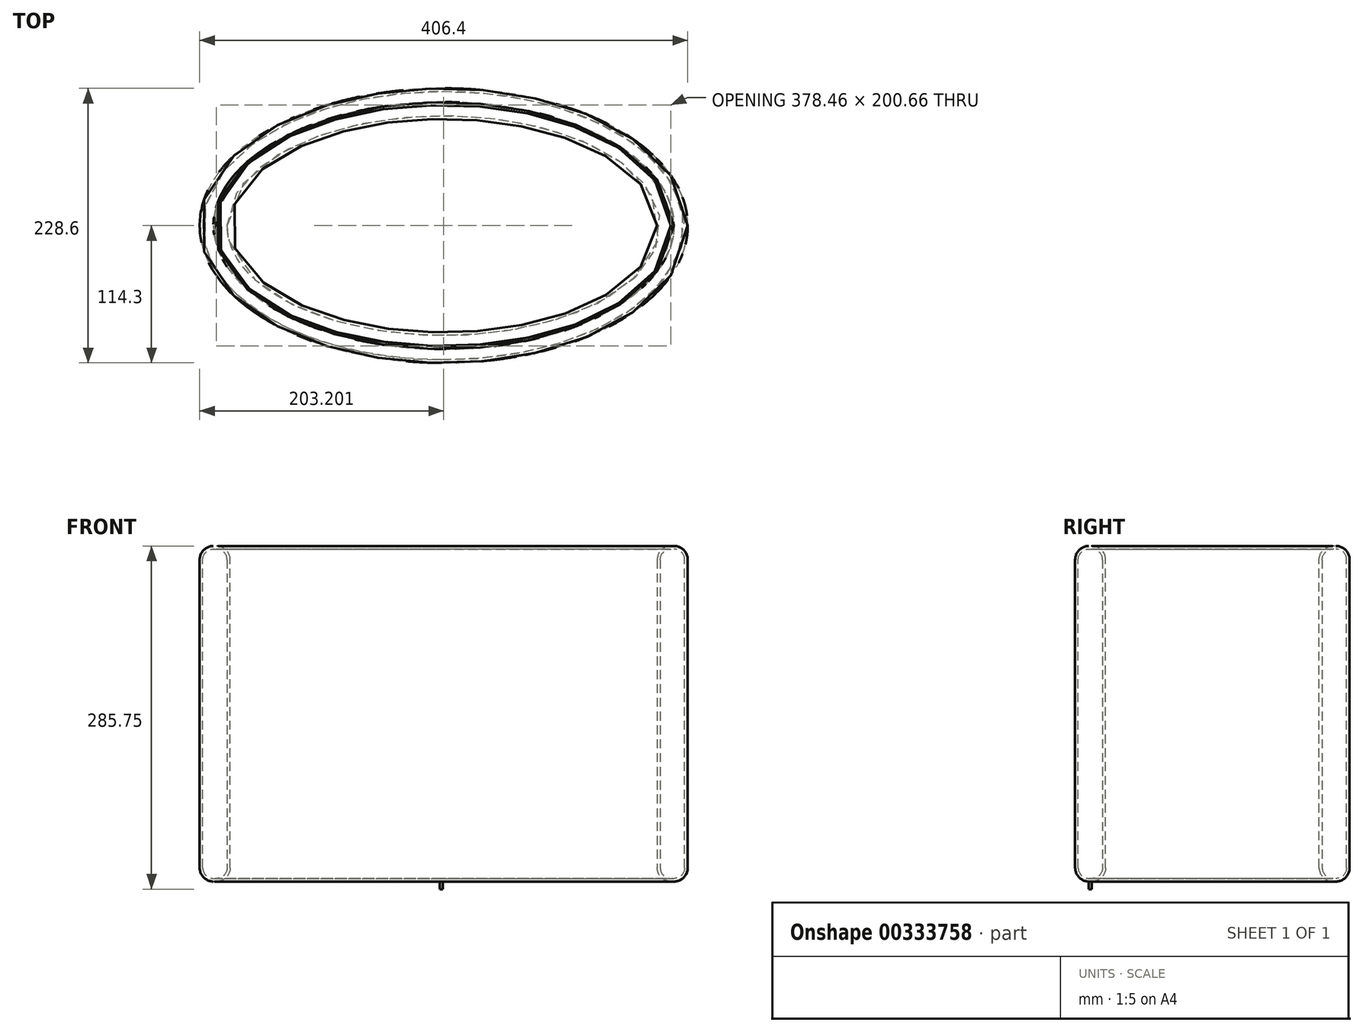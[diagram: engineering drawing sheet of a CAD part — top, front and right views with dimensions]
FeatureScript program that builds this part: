
annotation { "Feature Type Name" : "Feature", "Feature Type Description" : "" }
export const myFeature = defineFeature(function(context is Context, id is Id, definition is map)
    precondition{}
    {
        {
            var Q0;
            Q0=qCreatedBy(makeId("Top.planeOp"),FACE);
            var sketch = newSketch(context, id + "F0", { "sketchPlane" : qUnion([Q0])});
            skEllipse(sketch, "E0", {"center": v(0, 0) * mm, "majorRadius": 177.8 * mm, "minorRadius": 88.9 * mm, "majorAxis": v(1, 0)});
            skEllipse(sketch, "E1", {"center": v(0, 0) * mm, "majorRadius": 203.2 * mm, "minorRadius": 114.3 * mm, "majorAxis": v(1, 0)});
            skSolve(sketch);
        }
        {
            var Q0;
            Q0=makeQuery(id+"F0.imprint","IMPRINT",FACE,{"disambiguationData":[TD([[makeQuery(id+"F0.imprint","IMPRINT",EDGE,{"derivedFrom":sQuery(id+"F0.wireOp",EDGE,"E0")}),-1.0]])]});
            extrude(context, id + "F1", {"entities" : qUnion([Q0]), "depth" : 279.4 * mm});
        }
        {
            var Q0;
            Q0=makeQuery(id+"F1.opExtrude","CAP_FACE",FACE,{"disambiguationData":[OSD([sQuery(id+"F0.wireOp",EDGE,"E0"),sQuery(id+"F0.wireOp",EDGE,"E1")])],"isStart":false});
            var Q1;
            Q1=makeQuery(id+"F1.opExtrude","CAP_FACE",FACE,{"disambiguationData":[OSD([sQuery(id+"F0.wireOp",EDGE,"E0"),sQuery(id+"F0.wireOp",EDGE,"E1")])],"isStart":true});
            fillet(context, id + "F2", {"entities" : qUnion([Q0, Q1]), "radius" : 11.43 * mm, "tangentPropagation" : true, "allowEdgeOverflow" : false});
        }
        {
            var Q0;
            Q0=makeQuery(id+"F1.opExtrude","CAP_FACE",FACE,{"disambiguationData":[OSD([sQuery(id+"F0.wireOp",EDGE,"E0"),sQuery(id+"F0.wireOp",EDGE,"E1")])],"isStart":true});
            var sketch = newSketch(context, id + "F3", { "sketchPlane" : qUnion([Q0])});
            skCircle(sketch, "E2", {"center": v(-2.1, 101.6) * mm, "radius": 1.27 * mm});
            skPoint(sketch, "E2.first.point", {"position": v(-2.15, 102.86) * mm});
            skPoint(sketch, "E2.second.point", {"position": v(-2.04, 100.32) * mm});
            skPoint(sketch, "E2.third.point", {"position": v(-0.84, 101.41) * mm});
            skSolve(sketch);
        }
        {
            var Q0;
            Q0 = qSketchRegion(id + "F3", true);
            extrude(context, id + "F4", {"entities" : qUnion([Q0]), "operationType" : NewBodyOperationType.ADD, "depth" : 6.35 * mm, "hasSecondDirection" : true, "secondDirectionOppositeDirection" : true, "secondDirectionDepth" : 25.4 * mm});
        }
        {
            var Q0;
            Q0=makeQuery(id+"F1.opExtrude","SWEPT_FACE",FACE,{"disambiguationData":[OSD([sQuery(id+"F0.wireOp",EDGE,"E1")])]});
            var Q1;
            Q1=makeQuery(id+"F1.opExtrude","SWEPT_BODY",BODY,{"disambiguationData":[OSD([sQuery(id+"F0.wireOp",EDGE,"E0"),sQuery(id+"F0.wireOp",EDGE,"E1")])]});
            shell(context, id + "F5", {"isHollow" : true, "entities" : qUnion([Q0]), "parts" : qUnion([Q1]), "thickness" : 2.54 * mm});
        }
    });
